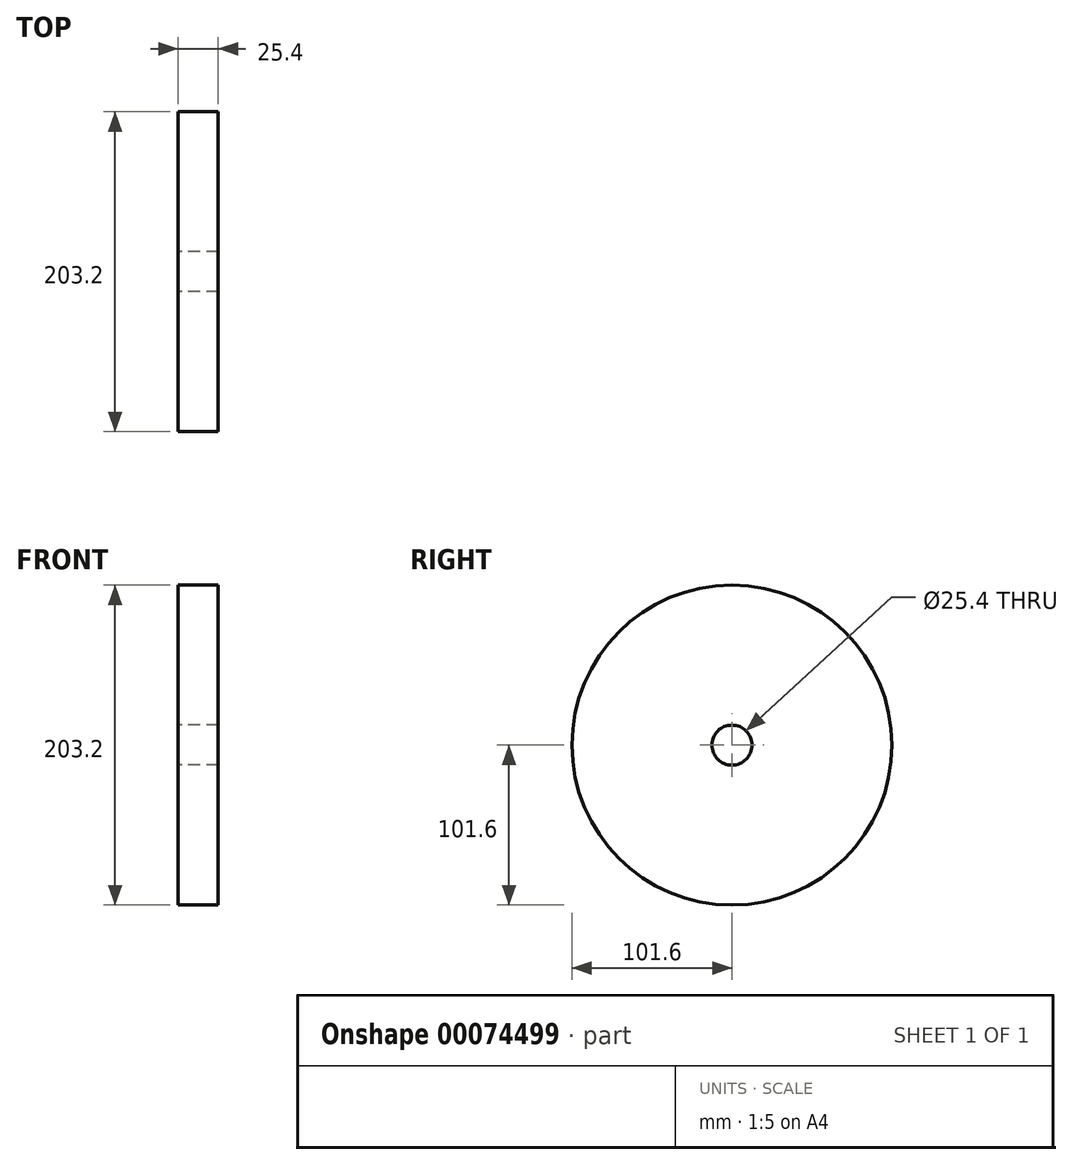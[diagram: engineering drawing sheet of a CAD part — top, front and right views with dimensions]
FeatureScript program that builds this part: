
annotation { "Feature Type Name" : "Feature", "Feature Type Description" : "" }
export const myFeature = defineFeature(function(context is Context, id is Id, definition is map)
    precondition{}
    {
        {
            var Q0;
            Q0=qCreatedBy(makeId("Right.planeOp"),FACE);
            var sketch = newSketch(context, id + "F0", { "sketchPlane" : qUnion([Q0])});
            skCircle(sketch, "E0", {"center": v(0, 0) * mm, "radius": 101.6 * mm});
            skCircle(sketch, "E1", {"center": v(0, 0) * mm, "radius": 12.7 * mm});
            skSolve(sketch);
        }
        {
            var Q0;
            Q0 = qSketchRegion(id + "F0", true);
            extrude(context, id + "F1", {"entities" : qUnion([Q0]), "depth" : 25.4 * mm, "offsetDistance" : 25.4 * mm});
        }
    });
